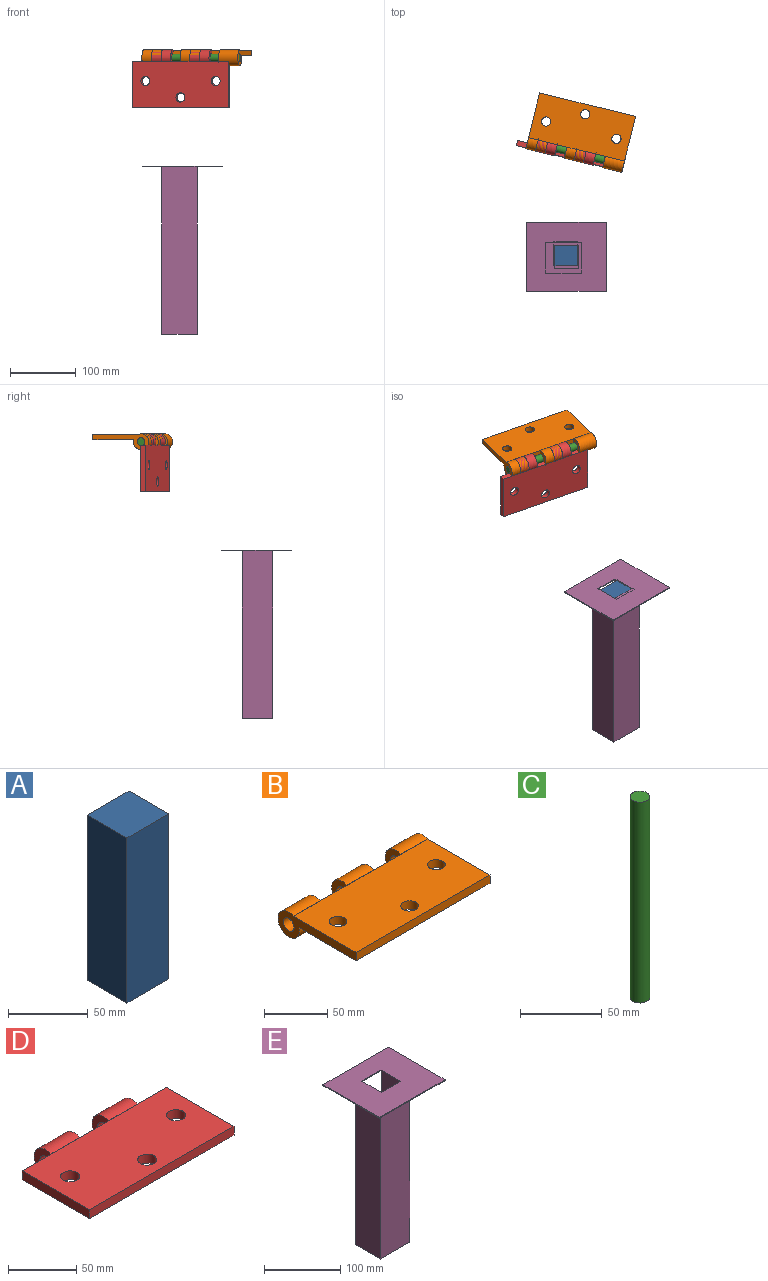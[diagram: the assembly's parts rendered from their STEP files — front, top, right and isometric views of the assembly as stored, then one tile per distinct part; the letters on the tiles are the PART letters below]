
ASSEMBLY  parts=5 mates=3
PART A: 6 faces, bbox 37.1x35.2x127 mm
  f0: plane 127x35.22mm, normal (-1,0,0), area 4472.5mm2, adj f1,f3,f4,f5
  f1: plane 127x37.07mm, normal (0,-1,0), area 4707.9mm2, adj f0,f2,f4,f5
  f2: plane 127x35.22mm, normal (1,0,0), area 4472.5mm2, adj f1,f3,f4,f5
  f3: plane 127x37.07mm, normal (0,1,0), area 4707.9mm2, adj f0,f2,f4,f5
  f4: plane 37.07x35.22mm, normal (0,0,1), area 1305.5mm2, adj f0,f1,f2,f3
  f5: plane 37.07x35.22mm, normal (0,0,-1), area 1305.5mm2, adj f0,f1,f2,f3
PART B: 19 faces, bbox 150x87.4x24 mm
  f0: plane 150x8mm, normal (0,1,0), area 481mm2, adj f1,f2,f3,f5,f6,f7,f9,f10
  f1: plane 150x70mm, normal (0,0,-1), area 9469.4mm2, adj f0,f2,f3,f4,f6,f7,f9,f10
  f2: plane 87.36x24mm, normal (1,0,0), area 866.3mm2, adj f0,f1,f4,f5,f6,f8
  f3: plane 87.36x24mm, normal (-1,0,0), area 866.3mm2, adj f0,f1,f4,f5,f14,f15
  f4: plane 150x8mm, normal (0,-1,0), area 1200mm2, adj f1,f2,f3,f5
  f5: plane 150x70mm, normal (0,0,1), area 10038.2mm2, adj f0,f2,f3,f4,f16,f17,f18
  f6: cylinder r=12mm len=30mm, axis (1,0,0), area 1946.3mm2, adj f0,f1,f2,f7
  f7: plane 24x24mm, normal (-1,0,0), area 306.3mm2, adj f0,f1,f6,f8
  f8: cylinder r=6mm len=30mm, axis (1,0,0), area 1131mm2, adj f2,f7
  f9: cylinder r=12mm len=30mm, axis (1,0,0), area 1946.3mm2, adj f0,f1,f10,f11
  f10: plane 24x24mm, normal (-1,0,0), area 306.3mm2, adj f0,f1,f9,f12
  f11: plane 24x24mm, normal (1,0,0), area 306.3mm2, adj f0,f1,f9,f12
  f12: cylinder r=6mm len=30mm, axis (1,0,0), area 1131mm2, adj f10,f11
  f13: plane 24x24mm, normal (1,0,0), area 306.3mm2, adj f0,f1,f14,f15
  f14: cylinder r=12mm len=30mm, axis (1,0,0), area 1946.3mm2, adj f0,f1,f3,f13
  f15: cylinder r=6mm len=30mm, axis (1,0,0), area 1131mm2, adj f3,f13
  f16: cylinder r=7mm len=14mm, axis (0,0,1), area 351.9mm2, adj f1,f5
  f17: cylinder r=7mm len=14mm, axis (0,0,1), area 351.9mm2, adj f1,f5
  f18: cylinder r=7mm len=14mm, axis (0,0,1), area 351.9mm2, adj f1,f5
PART C: 3 faces, bbox 12x12x150 mm
  f0: cylinder r=6mm len=150mm, axis (0,0,1), area 5654.9mm2, adj f1,f2
  f1: plane 12x12mm, normal (0,0,1), area 113.1mm2, adj f0
  f2: plane 12x12mm, normal (0,0,-1), area 113.1mm2, adj f0
PART D: 17 faces, bbox 150x87.4x24 mm
  f0: plane 150x8mm, normal (0,1,0), area 720.6mm2, adj f1,f2,f3,f5,f9,f10,f11,f13
  f1: plane 150x70mm, normal (0,0,-1), area 9659mm2, adj f0,f2,f3,f4,f6,f7,f8,f9
  f2: plane 70x8mm, normal (1,0,0), area 560mm2, adj f0,f1,f4,f5
  f3: plane 70x8mm, normal (-1,0,0), area 560mm2, adj f0,f1,f4,f5
  f4: plane 150x8mm, normal (0,-1,0), area 1200mm2, adj f1,f2,f3,f5
  f5: plane 150x70mm, normal (0,0,1), area 10038.2mm2, adj f0,f2,f3,f4,f6,f7,f8
  f6: cylinder r=7mm len=14mm, axis (0,0,1), area 351.9mm2, adj f1,f5
  f7: cylinder r=7mm len=14mm, axis (0,0,1), area 351.9mm2, adj f1,f5
  f8: cylinder r=7mm len=14mm, axis (0,0,1), area 351.9mm2, adj f1,f5
  f9: cylinder r=12mm len=30mm, axis (1,0,0), area 1946.3mm2, adj f0,f1,f10,f11
  f10: plane 24x24mm, normal (-1,0,0), area 306.3mm2, adj f0,f1,f9,f12
  f11: plane 24x24mm, normal (1,0,0), area 306.3mm2, adj f0,f1,f9,f12
  f12: cylinder r=6mm len=30mm, axis (1,0,0), area 1131mm2, adj f10,f11
  f13: cylinder r=12mm len=30mm, axis (1,0,0), area 1946.3mm2, adj f0,f1,f14,f15
  f14: plane 24x24mm, normal (-1,0,0), area 306.3mm2, adj f0,f1,f13,f16
  f15: plane 24x24mm, normal (1,0,0), area 306.3mm2, adj f0,f1,f13,f16
  f16: cylinder r=6mm len=30mm, axis (1,0,0), area 1131mm2, adj f14,f15
PART E: 16 faces, bbox 121.1x105x255.3 mm
  f0: plane 254x46.65mm, normal (-1,0,0), area 11848.3mm2, adj f1,f3,f4,f5
  f1: plane 254x54.37mm, normal (0,-1,0), area 13809.9mm2, adj f0,f2,f4,f5
  f2: plane 254x46.65mm, normal (1,0,0), area 11848.3mm2, adj f1,f3,f4,f5
  f3: plane 254x54.37mm, normal (0,1,0), area 9343.3mm2, adj f0,f2,f4,f5,f11,f12,f13
  f4: plane 54.37x46.65mm, normal (0,0,-1), area 2536.2mm2, adj f0,f1,f2,f3
  f5: plane 121.1x105.03mm, normal (0,0,-1), area 10160.9mm2, adj f0,f1,f2,f3,f6,f7,f8,f9
  f6: plane 105.03x1.27mm, normal (-1,0,0), area 133.4mm2, adj f5,f7,f9,f10
  f7: plane 121.1x1.27mm, normal (0,-1,0), area 153.8mm2, adj f5,f6,f8,f10
  f8: plane 105.03x1.27mm, normal (1,0,0), area 133.4mm2, adj f5,f7,f9,f10
  f9: plane 121.1x1.27mm, normal (0,1,0), area 153.8mm2, adj f5,f6,f8,f10
  f10: plane 121.1x105.03mm, normal (0,0,1), area 11435mm2, adj f6,f7,f8,f9,f12,f13,f14,f15
  f11: plane 35.53x35.53mm, normal (0,0,1), area 1262.1mm2, adj f3,f12,f13,f15
  f12: plane 127x36.14mm, normal (1,0,0), area 4512.5mm2, adj f3,f5,f10,f11,f14,f15
  f13: plane 127x36.14mm, normal (-1,0,0), area 4512.5mm2, adj f3,f5,f10,f11,f14,f15
  f14: plane 35.53x1.27mm, normal (0,-1,0), area 45.1mm2, adj f5,f10,f12,f13
  f15: plane 127x35.53mm, normal (0,1,0), area 4511.8mm2, adj f10,f11,f12,f13
PLACE A rot(axis=(0,0,1),180deg) t=(-35.96,-78.69,-274.76)mm
PLACE B rot(axis=(0,0,1),166.2deg) t=(1.94,109.66,23.55)mm
PLACE C rot(axis=(-0.7,0.09,0.7),170.2deg) t=(-70.88,127.61,10.05)mm
PLACE D rot(axis=(0.99,-0.12,-0.12),90.8deg) t=(-23.9,67.51,-23.56)mm
PLACE E t=(-24.65,-88.11,-149.03)mm
MATE revolute D.f9 <-> C.f0  axis (0.97,-0.24,0) through (-7.72,70.47,16.8)mm
MATE revolute C.f0 <-> B.f6  axis (-0.97,0.24,0) through (-80.54,88.42,16.8)mm
MATE slider A.f4 <-> E.f10  axis (0,0,1) through (-21.75,-87.34,-147.76)mm
